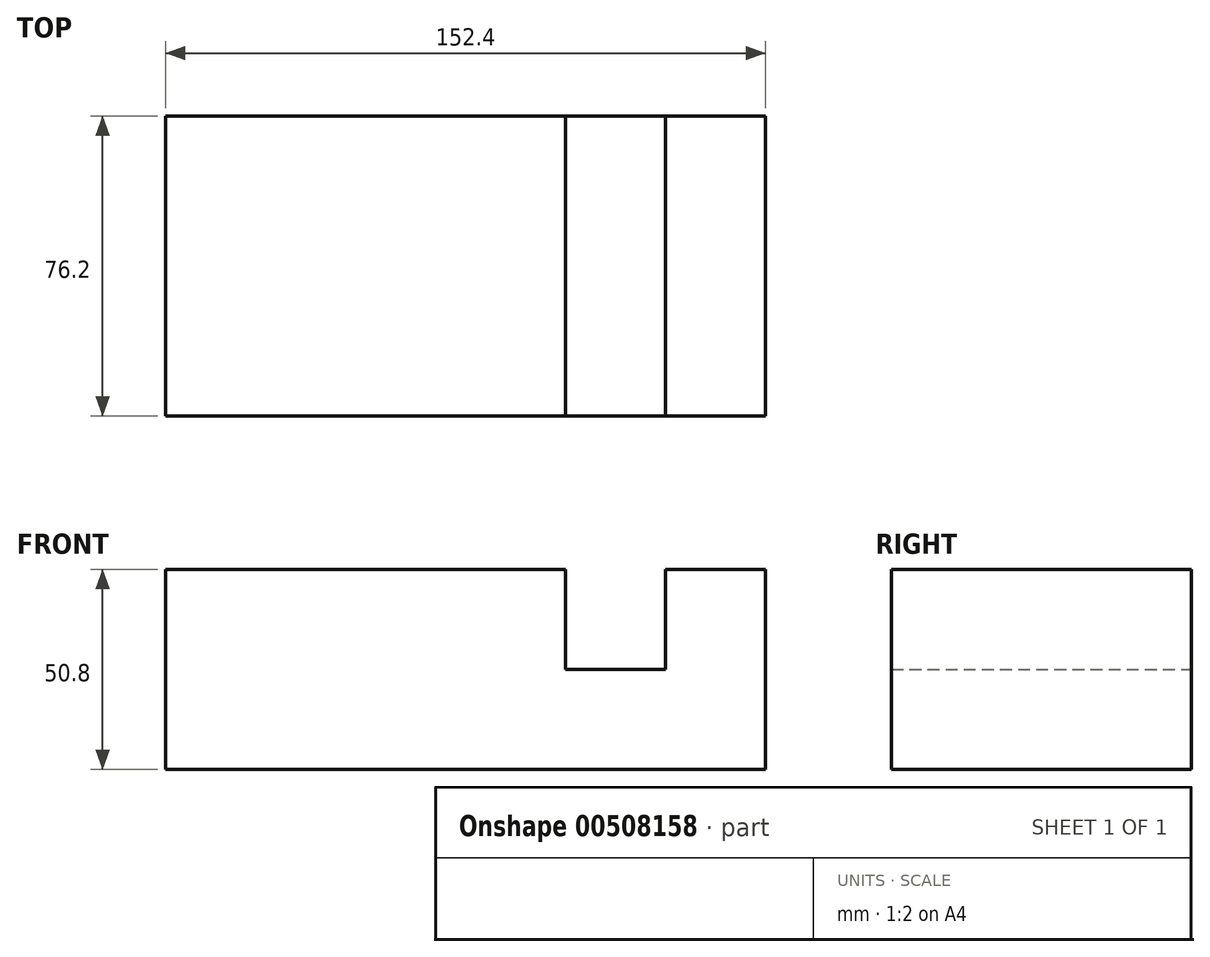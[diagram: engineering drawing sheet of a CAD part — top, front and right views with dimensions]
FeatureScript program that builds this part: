
annotation { "Feature Type Name" : "Feature", "Feature Type Description" : "" }
export const myFeature = defineFeature(function(context is Context, id is Id, definition is map)
    precondition{}
    {
        {
            var Q0;
            Q0=qCreatedBy(makeId("Front.planeOp"),FACE);
            var sketch = newSketch(context, id + "F0", { "sketchPlane" : qUnion([Q0])});
            skLineSegment(sketch, "E0", {"start": v(-34.52, 30.82) * mm, "end": v(67.08, 30.82) * mm});
            skLineSegment(sketch, "E1", {"start": v(67.08, 5.42) * mm, "end": v(92.48, 5.42) * mm});
            skLineSegment(sketch, "E2", {"start": v(92.48, 5.42) * mm, "end": v(92.48, 30.82) * mm});
            skLineSegment(sketch, "E3", {"start": v(117.88, 30.82) * mm, "end": v(117.88, -19.98) * mm});
            skLineSegment(sketch, "E4", {"start": v(117.88, -19.98) * mm, "end": v(-34.52, -19.98) * mm});
            skLineSegment(sketch, "E5", {"start": v(-34.52, -19.98) * mm, "end": v(-34.52, 30.82) * mm});
            skLineSegment(sketch, "E6", {"start": v(92.48, 30.82) * mm, "end": v(117.88, 30.82) * mm});
            skLineSegment(sketch, "E7", {"start": v(67.08, 30.82) * mm, "end": v(67.08, 5.42) * mm});
            skSolve(sketch);
        }
        {
            var Q0;
            Q0 = qSketchRegion(id + "F0", true);
            extrude(context, id + "F1", {"entities" : qUnion([Q0]), "depth" : 76.2 * mm});
        }
    });
